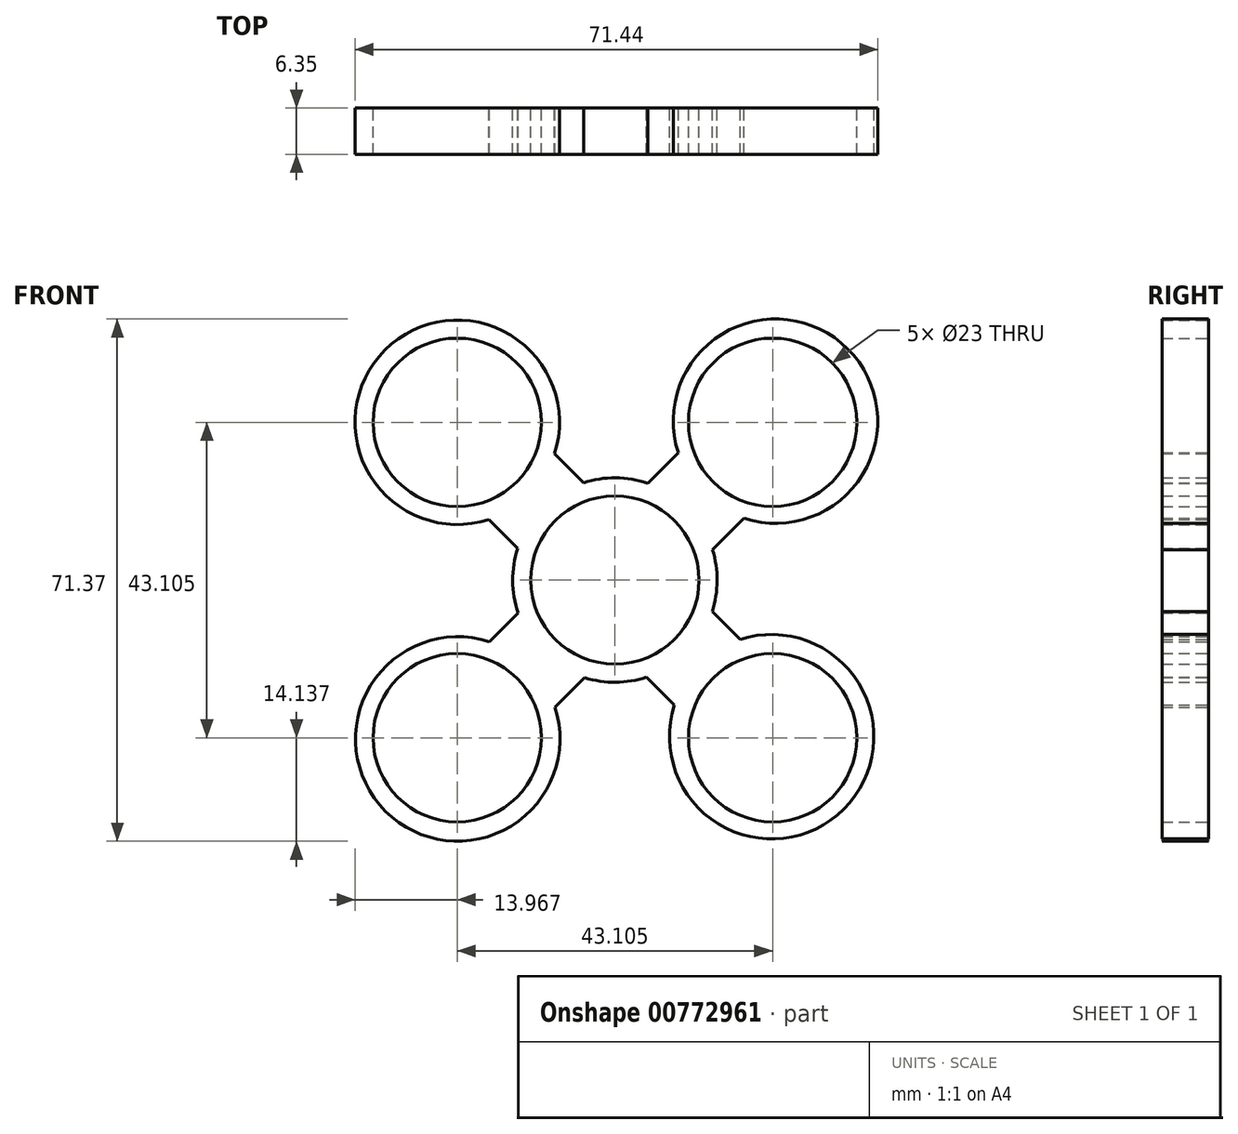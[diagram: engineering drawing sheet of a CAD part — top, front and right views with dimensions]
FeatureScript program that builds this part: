
annotation { "Feature Type Name" : "Feature", "Feature Type Description" : "" }
export const myFeature = defineFeature(function(context is Context, id is Id, definition is map)
    precondition{}
    {
        {
            var Q0;
            Q0=qCreatedBy(makeId("Front.planeOp"),FACE);
            var sketch = newSketch(context, id + "F0", { "sketchPlane" : qUnion([Q0])});
            skCircle(sketch, "E0", {"center": v(0, 0) * mm, "radius": 11.5 * mm});
            skCircle(sketch, "E1", {"center": v(21.55, -21.55) * mm, "radius": 11.5 * mm});
            skCircle(sketch, "E2", {"center": v(-21.55, -21.55) * mm, "radius": 11.5 * mm});
            skCircle(sketch, "E3", {"center": v(-21.55, 21.55) * mm, "radius": 11.5 * mm});
            skCircle(sketch, "E4", {"center": v(21.55, 21.55) * mm, "radius": 11.5 * mm});
            skSolve(sketch);
        }
        {
            var Q0;
            Q0=qCreatedBy(makeId("Front.planeOp"),FACE);
            var sketch = newSketch(context, id + "F1", { "sketchPlane" : qUnion([Q0])});
            skPoint(sketch, "E5.middle", {"position": v(0, 0) * mm});
            skLineSegment(sketch, "E6", {"start": v(-21.48, -21.72) * mm, "end": v(21.95, 21.71) * mm});
            skLineSegment(sketch, "E7", {"start": v(-21.55, 21.56) * mm, "end": v(21.42, -21.41) * mm});
            skArc(sketch, "E8.0.startCap", {"start": v(-17, -26.2) * mm, "mid": v(-25.97, -26.2) * mm, "end": v(-25.97, -17.23) * mm});
            skArc(sketch, "E8.0.endCap", {"start": v(17.46, 26.2) * mm, "mid": v(26.44, 26.2) * mm, "end": v(26.44, 17.22) * mm});
            skLineSegment(sketch, "E8.0.left", {"start": v(-25.97, -17.23) * mm, "end": v(17.46, 26.2) * mm});
            skLineSegment(sketch, "E8.0.right", {"start": v(-17, -26.2) * mm, "end": v(26.44, 17.22) * mm});
            skArc(sketch, "E8.1.startCap", {"start": v(-26.04, 17.07) * mm, "mid": v(-26.04, 26.05) * mm, "end": v(-17.06, 26.05) * mm});
            skArc(sketch, "E8.1.endCap", {"start": v(25.91, -16.92) * mm, "mid": v(25.91, -25.9) * mm, "end": v(16.93, -25.9) * mm});
            skLineSegment(sketch, "E8.1.left", {"start": v(-17.06, 26.05) * mm, "end": v(25.91, -16.92) * mm});
            skLineSegment(sketch, "E8.1.right", {"start": v(-26.04, 17.07) * mm, "end": v(16.93, -25.9) * mm});
            skCircle(sketch, "E9", {"center": v(-21.55, 21.56) * mm, "radius": 13.97 * mm});
            skCircle(sketch, "E10", {"center": v(21.95, 21.71) * mm, "radius": 13.97 * mm});
            skCircle(sketch, "E11", {"center": v(21.42, -21.41) * mm, "radius": 13.97 * mm});
            skCircle(sketch, "E12", {"center": v(-21.48, -21.72) * mm, "radius": 13.97 * mm});
            skCircle(sketch, "E13", {"center": v(0, 0) * mm, "radius": 13.97 * mm});
            skSolve(sketch);
        }
        {
            var Q0;
            Q0 = qSketchRegion(id + "F1", true);
            extrude(context, id + "F2", {"entities" : qUnion([Q0]), "depth" : 6.35 * mm, "offsetDistance" : 25.4 * mm});
        }
        {
            var Q0;
            Q0 = qSketchRegion(id + "F0", true);
            extrude(context, id + "F3", {"entities" : qUnion([Q0]), "operationType" : NewBodyOperationType.REMOVE, "depth" : 6.35 * mm, "offsetDistance" : 25.4 * mm});
        }
    });
